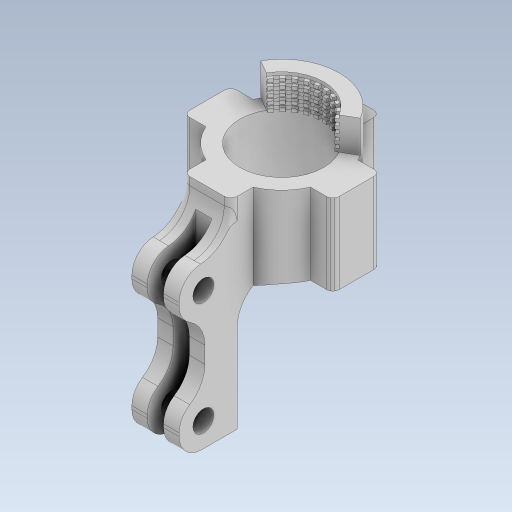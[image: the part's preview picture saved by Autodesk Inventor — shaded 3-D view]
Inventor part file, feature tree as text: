
AUTODESK INVENTOR PART (.ipt)
format: ipt  version: 2023 (Build 270158000, 158)  size: 1,204,736 bytes
history: native  units: in
note: dims shown in document units (in); Inventor stores cm internally (conversion verified against a paired STEP export)
features: sketch x6, extrude x5, projected_geometry x2, revolve x1, fillet x1
ambient origin geometry x8: Origin, YZ Plane, XZ Plane, XY Plane, X Axis, Y Axis, Z Axis, Center Point
bodies: Solid1 (feature_tree)
feature tree (15):
  extrude  "Extrusion1"  Depth=0.9843in TaperAngle=0.0deg
  extrude  "Extrusion2"  Depth=0.3937in TaperAngle=0.0deg
  extrude  "Extrusion3"  Depth=7.874in TaperAngle=120.0deg
  revolve  "Revolution1"  [1 undecoded]
  extrude  "Extrusion14"  Depth=1.9685in
  fillet  "Fillet3"  Radius=0.2559in
  extrude  "Extrusion15"  Depth=0.3937in
  sketch  "Sketch1"  dims[d0=1.0236in d1=0.9843in d2=0.0in]
  sketch  "Sketch2"  dims[d3=120.0deg d4=0.3937in d5=0.0in]
  sketch  "Sketch3"  dims[d6=0.0394in d7=7.874in d9=120.0deg]
  sketch  "Sketch4"  dims[d11=0.3937in d12=0.0in d14=3.937in d16=0.0394in d17=0.3937in d19=0.3937in]
  sketch  "Sketch26"  dims[d21=360.0deg d107=1.9685in d108=0.2559in]
  sketch  "Sketch27"  dims[d109=1.378in d111=0.3937in d112=0.9843in d113=0.9843in d114=0.0in d115=0.2756in d116=0.3937in d117=0.1969in d118=0.5906in d119=0.0in d91=0.0344in d92=0.0344in d93=0.0197in d94=0.0344in]
  projected_geometry  "Projected Loop10"
  projected_geometry  "Projected Loop11"
note: 1 required parameter value undecoded (feature->parameter linkage not recoverable at this tier; creation-order binding heuristic only, values carry confidence <= 0.55)
